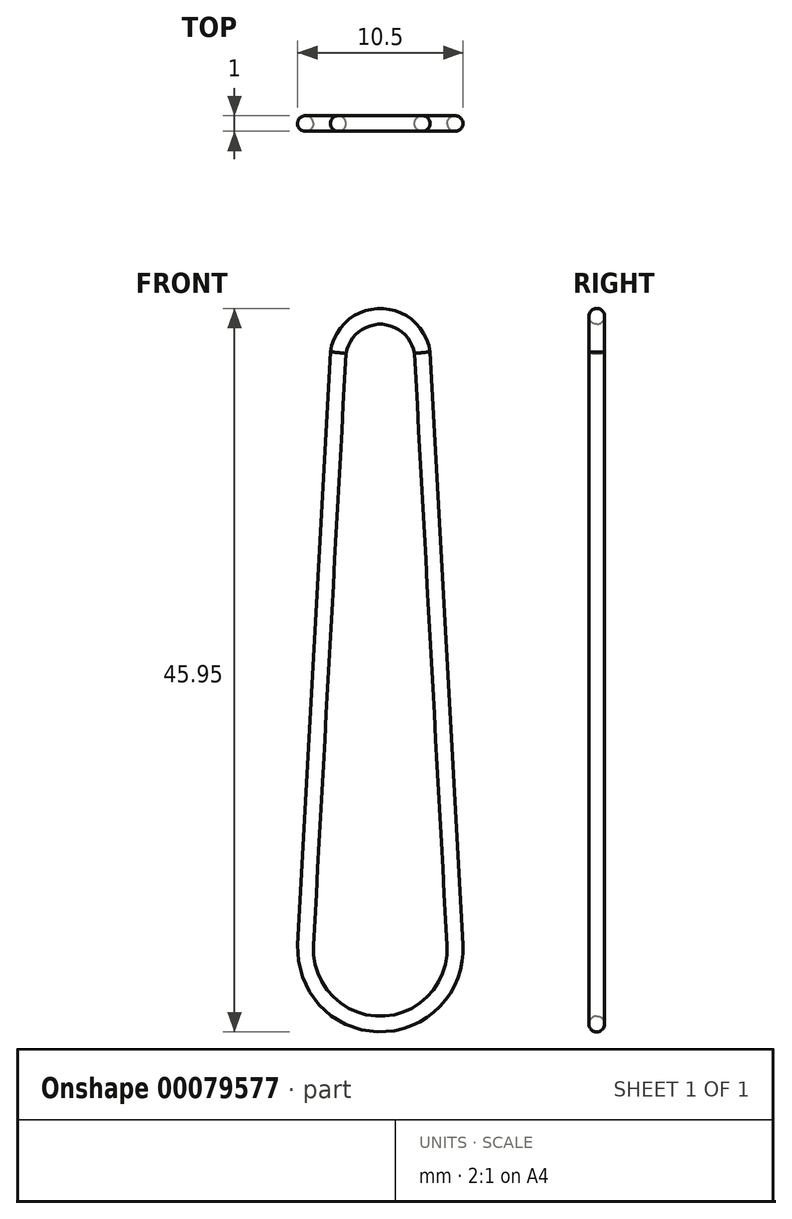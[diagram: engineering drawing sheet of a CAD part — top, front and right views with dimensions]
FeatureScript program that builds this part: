
annotation { "Feature Type Name" : "Feature", "Feature Type Description" : "" }
export const myFeature = defineFeature(function(context is Context, id is Id, definition is map)
    precondition{}
    {
        {
            var Q0;
            Q0=qCreatedBy(makeId("Front.planeOp"),FACE);
            var sketch = newSketch(context, id + "F0", { "sketchPlane" : qUnion([Q0])});
            skLineSegment(sketch, "E0", {"start": v(-2.67, 33.14) * mm, "end": v(-4.74, -4.49) * mm});
            skLineSegment(sketch, "E1.MirrorCS", {"start": v(2.67, 33.14) * mm, "end": v(4.74, -4.49) * mm});
            skArc(sketch, "E2", {"start": v(4.74, -4.49) * mm, "mid": v(0, 0) * mm, "end": v(-4.74, -4.49) * mm, "construction": true});
            skArc(sketch, "E3", {"start": v(-4.74, -4.49) * mm, "mid": v(0, -9.5) * mm, "end": v(4.74, -4.49) * mm});
            skArc(sketch, "E4", {"start": v(2.67, 33.14) * mm, "mid": v(0, 35.45) * mm, "end": v(-2.67, 33.14) * mm});
            skArc(sketch, "E5", {"start": v(-2.67, 33.14) * mm, "mid": v(0, 30.05) * mm, "end": v(2.67, 33.14) * mm, "construction": true});
            skLineSegment(sketch, "E6", {"start": v(-2.67, 33.14) * mm, "end": v(2.67, 33.14) * mm, "construction": true});
            skPoint(sketch, "E7", {"position": v(0, 35.45) * mm});
            skSolve(sketch);
        }
        {
            var Q0;
            Q0=qCreatedBy(makeId("Right.planeOp"),FACE);
            var sketch = newSketch(context, id + "F1", { "sketchPlane" : qUnion([Q0])});
            skCircle(sketch, "E8", {"center": v(0, 35.45) * mm, "radius": 0.5 * mm});
            skSolve(sketch);
        }
        {
            var Q0;
            Q0=makeQuery(id+"F1.imprint","IMPRINT",FACE,{"disambiguationData":[TD([[makeQuery(id+"F1.imprint","IMPRINT",EDGE,{"derivedFrom":sQuery(id+"F1.wireOp",EDGE,"E8")}),1.0]])]});
            var Q1;
            Q1=sQuery(id+"F0.wireOp",EDGE,"E4");
            var Q2;
            Q2=sQuery(id+"F0.wireOp",EDGE,"E1.MirrorCS");
            var Q3;
            Q3=sQuery(id+"F0.wireOp",EDGE,"E0");
            var Q4;
            Q4=sQuery(id+"F0.wireOp",EDGE,"E3");
            sweep(context, id + "F2", {"profiles" : qUnion([Q0]), "path" : qUnion([Q1, Q2, Q3, Q4])});
        }
    });
